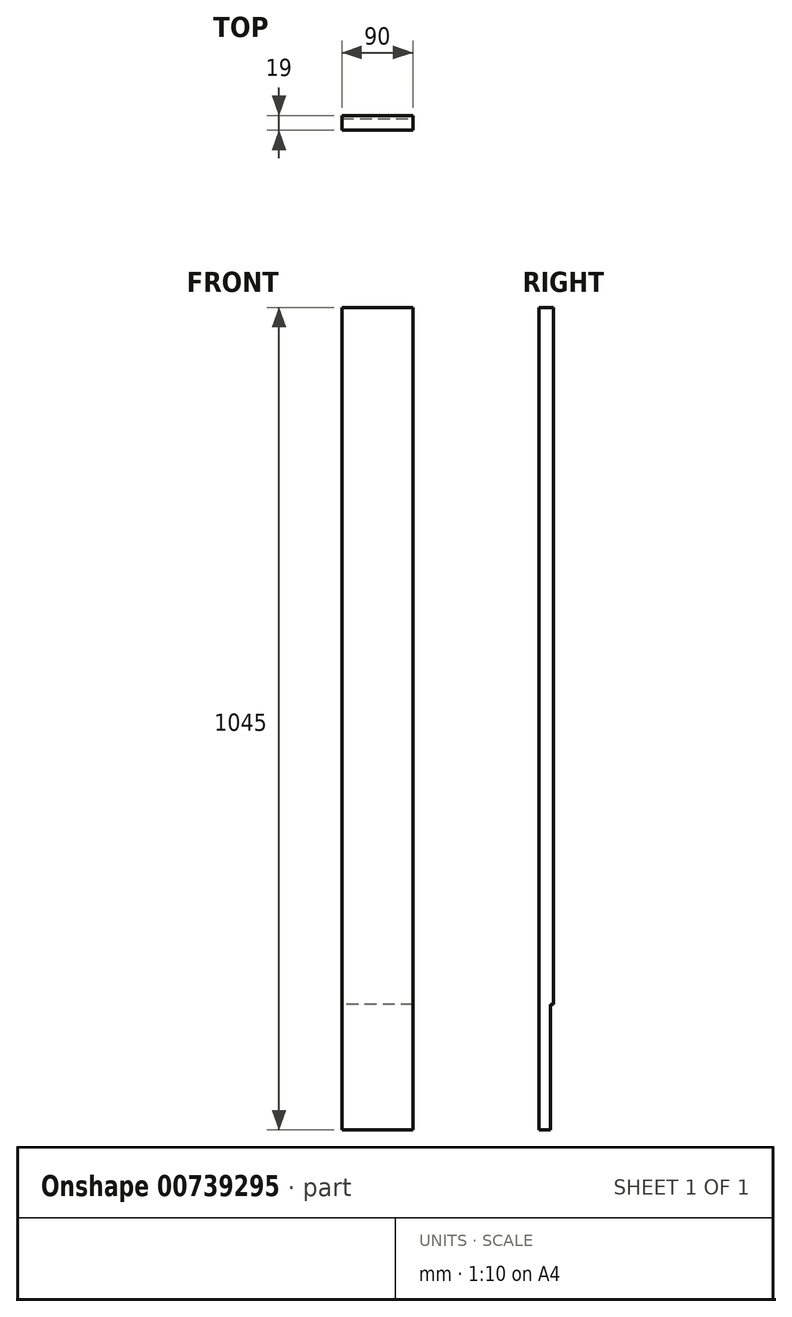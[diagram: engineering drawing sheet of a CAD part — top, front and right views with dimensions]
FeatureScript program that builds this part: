
annotation { "Feature Type Name" : "Feature", "Feature Type Description" : "" }
export const myFeature = defineFeature(function(context is Context, id is Id, definition is map)
    precondition{}
    {
        {
            var Q0;
            Q0=qCreatedBy(makeId("Top.planeOp"),FACE);
            var sketch = newSketch(context, id + "F0", { "sketchPlane" : qUnion([Q0])});
            skLineSegment(sketch, "E0.bottom", {"start": v(0, 0) * mm, "end": v(90, 0) * mm});
            skLineSegment(sketch, "E0.top", {"start": v(0, 19) * mm, "end": v(90, 19) * mm});
            skLineSegment(sketch, "E0.left", {"start": v(0, 0) * mm, "end": v(0, 19) * mm});
            skLineSegment(sketch, "E0.right", {"start": v(90, 0) * mm, "end": v(90, 19) * mm});
            skSolve(sketch);
        }
        {
            var Q0;
            Q0=makeQuery(id+"F0.imprint","IMPRINT",FACE,{"disambiguationData":[TD([[makeQuery(id+"F0.imprint","IMPRINT",EDGE,{"derivedFrom":sQuery(id+"F0.wireOp",EDGE,"E0.bottom")}),1.0]])]});
            extrude(context, id + "F1", {"entities" : qUnion([Q0]), "depth" : 1045 * mm, "offsetDistance" : 25 * mm});
        }
        {
            var Q0;
            Q0=makeQuery(id+"F1.opExtrude","SWEPT_FACE",FACE,{"disambiguationData":[OSD([sQuery(id+"F0.wireOp",EDGE,"E0.top")])]});
            var sketch = newSketch(context, id + "F2", { "sketchPlane" : qUnion([Q0])});
            skLineSegment(sketch, "E1", {"start": v(-90, 160) * mm, "end": v(0, 160) * mm});
            skSolve(sketch);
        }
        {
            var Q0;
            {var subQ0=sQuery(id+"F2.wireOp",EDGE,"E1");Q0=makeQuery(id+"F2.imprint","IMPRINT",FACE,{"disambiguationData":[TD([[makeQuery(id+"F2.imprint","IMPRINT",EDGE,{"derivedFrom":subQ0}),-1.0]])]});}
            extrude(context, id + "F3", {"entities" : qUnion([Q0]), "operationType" : NewBodyOperationType.REMOVE, "oppositeDirection" : true, "depth" : 4 * mm, "offsetDistance" : 25 * mm});
        }
    });
